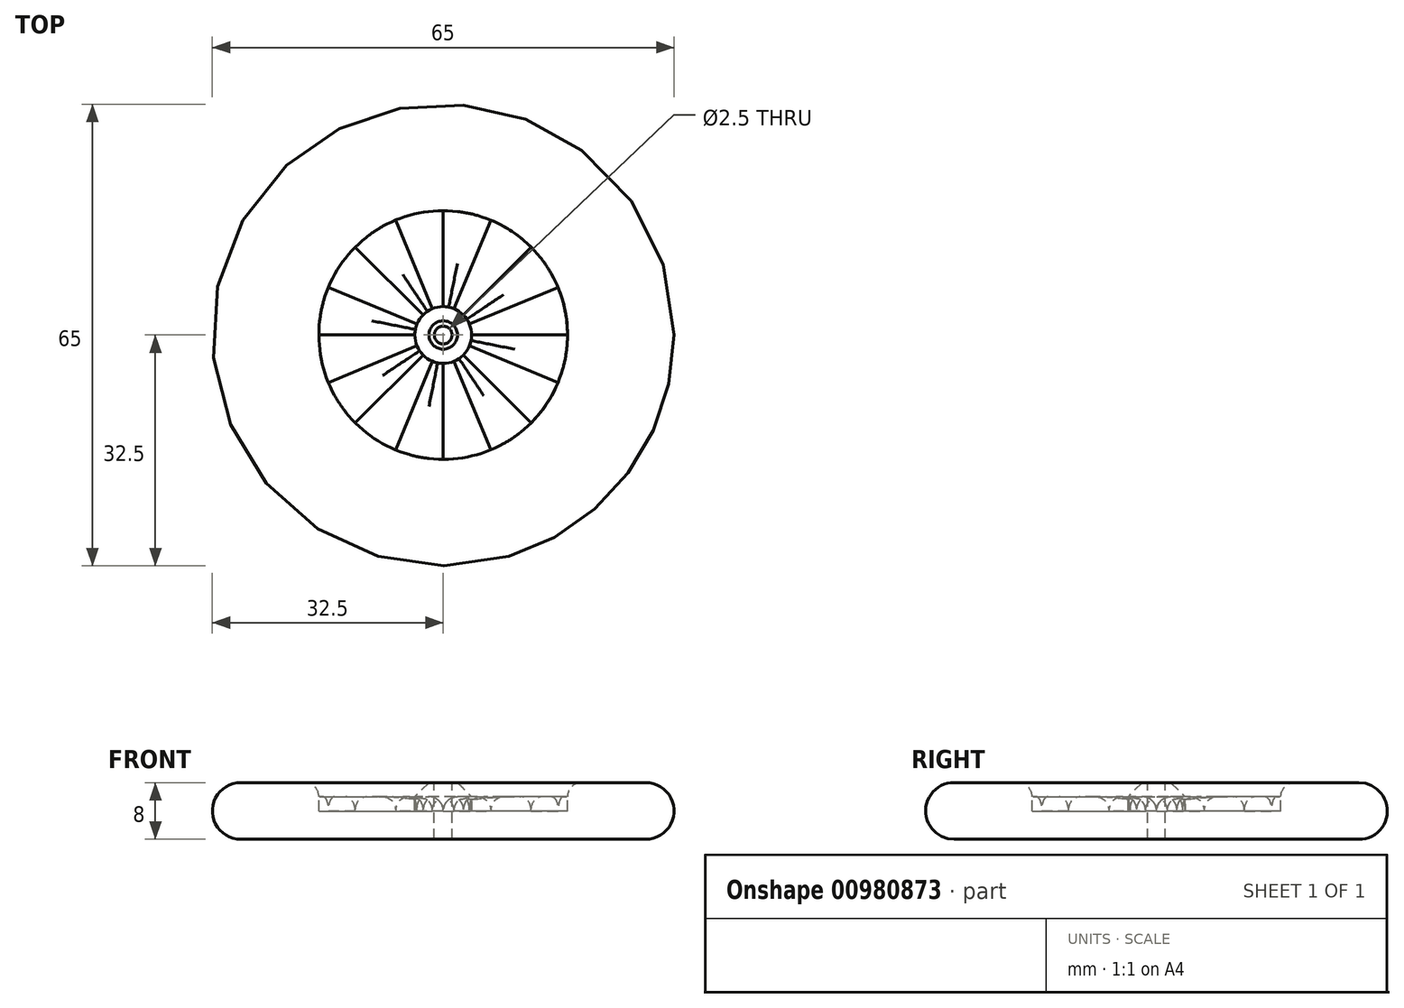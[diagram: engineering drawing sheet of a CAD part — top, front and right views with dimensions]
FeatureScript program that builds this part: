
annotation { "Feature Type Name" : "Feature", "Feature Type Description" : "" }
export const myFeature = defineFeature(function(context is Context, id is Id, definition is map)
    precondition{}
    {
        {
            var Q0;
            Q0=qCreatedBy(makeId("Top.planeOp"),FACE);
            var sketch = newSketch(context, id + "F0", { "sketchPlane" : qUnion([Q0])});
            skCircle(sketch, "E0", {"center": v(0, 0) * mm, "radius": 1.25 * mm});
            skCircle(sketch, "E1", {"center": v(0, 0) * mm, "radius": 4 * mm});
            skCircle(sketch, "E2", {"center": v(0, 0) * mm, "radius": 32.5 * mm});
            skCircle(sketch, "E3", {"center": v(0, 0) * mm, "radius": 17.5 * mm});
            skLineSegment(sketch, "E4", {"start": v(0, 17.5) * mm, "end": v(0, 4) * mm});
            skLineSegment(sketch, "E5.1.0", {"start": v(-6.7, 16.17) * mm, "end": v(-1.53, 3.7) * mm});
            skLineSegment(sketch, "E5.2.0", {"start": v(-12.37, 12.37) * mm, "end": v(-2.83, 2.83) * mm});
            skLineSegment(sketch, "E5.3.0", {"start": v(-16.17, 6.7) * mm, "end": v(-3.7, 1.53) * mm});
            skLineSegment(sketch, "E5.4.0", {"start": v(-17.5, 0) * mm, "end": v(-4, 0) * mm});
            skLineSegment(sketch, "E5.5.0", {"start": v(-16.17, -6.7) * mm, "end": v(-3.7, -1.53) * mm});
            skLineSegment(sketch, "E5.6.0", {"start": v(-12.37, -12.37) * mm, "end": v(-2.83, -2.83) * mm});
            skLineSegment(sketch, "E5.7.0", {"start": v(-6.7, -16.17) * mm, "end": v(-1.53, -3.7) * mm});
            skLineSegment(sketch, "E5.8.0", {"start": v(0, -17.5) * mm, "end": v(0, -4) * mm});
            skLineSegment(sketch, "E5.9.0", {"start": v(6.7, -16.17) * mm, "end": v(1.53, -3.7) * mm});
            skLineSegment(sketch, "E5.10.0", {"start": v(12.37, -12.37) * mm, "end": v(2.83, -2.83) * mm});
            skLineSegment(sketch, "E5.11.0", {"start": v(16.17, -6.7) * mm, "end": v(3.7, -1.53) * mm});
            skLineSegment(sketch, "E5.12.0", {"start": v(17.5, 0) * mm, "end": v(4, 0) * mm});
            skLineSegment(sketch, "E5.13.0", {"start": v(16.17, 6.7) * mm, "end": v(3.7, 1.53) * mm});
            skLineSegment(sketch, "E5.14.0", {"start": v(12.37, 12.37) * mm, "end": v(2.83, 2.83) * mm});
            skLineSegment(sketch, "E5.15.0", {"start": v(6.7, 16.17) * mm, "end": v(1.53, 3.7) * mm});
            skSolve(sketch);
        }
        {
            var Q0;
            Q0=makeQuery(id+"F0.imprint","IMPRINT",FACE,{"disambiguationData":[TD([[makeQuery(id+"F0.imprint","IMPRINT",EDGE,{"derivedFrom":sQuery(id+"F0.wireOp",EDGE,"E2")}),1.0]])]});
            var Q1;
            Q1=makeQuery(id+"F0.imprint","IMPRINT",FACE,{"disambiguationData":[TD([[makeQuery(id+"F0.imprint","IMPRINT",EDGE,{"derivedFrom":sQuery(id+"F0.wireOp",EDGE,"E0")}),-1.0]])]});
            extrude(context, id + "F1", {"entities" : qUnion([Q0, Q1]), "endBound" : BoundingType.SYMMETRIC, "oppositeDirection" : true, "depth" : 8 * mm, "offsetDistance" : 25 * mm});
        }
        {
            var Q0;
            Q0=makeQuery(id+"F0.imprint","IMPRINT",FACE,{"disambiguationData":[TD([[makeQuery(id+"F0.imprint","IMPRINT",EDGE,{"derivedFrom":sQuery(id+"F0.wireOp",EDGE,"E1")}),-1.0]])]});
            extrude(context, id + "F2", {"entities" : qUnion([Q0]), "operationType" : NewBodyOperationType.ADD, "oppositeDirection" : true, "depth" : 4 * mm, "offsetDistance" : 25 * mm});
        }
        {
            var Q0;
            {var subQ0=sQuery(id+"F0.wireOp",EDGE,"E5.3.0");Q0=makeQuery(id+"F0.imprint","IMPRINT",FACE,{"disambiguationData":[TD([[makeQuery(id+"F0.imprint","IMPRINT",EDGE,{"derivedFrom":subQ0}),-1.0]])]});}
            var Q1;
            {var subQ0=sQuery(id+"F0.wireOp",EDGE,"E5.1.0");Q1=makeQuery(id+"F0.imprint","IMPRINT",FACE,{"disambiguationData":[TD([[makeQuery(id+"F0.imprint","IMPRINT",EDGE,{"derivedFrom":subQ0}),-1.0]])]});}
            var Q2;
            {var subQ0=sQuery(id+"F0.wireOp",EDGE,"E4");Q2=makeQuery(id+"F0.imprint","IMPRINT",FACE,{"disambiguationData":[TD([[makeQuery(id+"F0.imprint","IMPRINT",EDGE,{"derivedFrom":subQ0}),1.0]])]});}
            var Q3;
            {var subQ0=sQuery(id+"F0.wireOp",EDGE,"E5.13.0");Q3=makeQuery(id+"F0.imprint","IMPRINT",FACE,{"disambiguationData":[TD([[makeQuery(id+"F0.imprint","IMPRINT",EDGE,{"derivedFrom":subQ0}),-1.0]])]});}
            var Q4;
            {var subQ0=sQuery(id+"F0.wireOp",EDGE,"E5.11.0");Q4=makeQuery(id+"F0.imprint","IMPRINT",FACE,{"disambiguationData":[TD([[makeQuery(id+"F0.imprint","IMPRINT",EDGE,{"derivedFrom":subQ0}),-1.0]])]});}
            var Q5;
            {var subQ0=sQuery(id+"F0.wireOp",EDGE,"E5.9.0");Q5=makeQuery(id+"F0.imprint","IMPRINT",FACE,{"disambiguationData":[TD([[makeQuery(id+"F0.imprint","IMPRINT",EDGE,{"derivedFrom":subQ0}),-1.0]])]});}
            var Q6;
            {var subQ0=sQuery(id+"F0.wireOp",EDGE,"E5.7.0");Q6=makeQuery(id+"F0.imprint","IMPRINT",FACE,{"disambiguationData":[TD([[makeQuery(id+"F0.imprint","IMPRINT",EDGE,{"derivedFrom":subQ0}),-1.0]])]});}
            var Q7;
            {var subQ0=sQuery(id+"F0.wireOp",EDGE,"E5.5.0");Q7=makeQuery(id+"F0.imprint","IMPRINT",FACE,{"disambiguationData":[TD([[makeQuery(id+"F0.imprint","IMPRINT",EDGE,{"derivedFrom":subQ0}),-1.0]])]});}
            extrude(context, id + "F3", {"entities" : qUnion([Q0, Q1, Q2, Q3, Q4, Q5, Q6, Q7]), "operationType" : NewBodyOperationType.ADD, "depth" : 2 * mm, "offsetDistance" : 25 * mm});
        }
        {
            var Q0;
            Q0=makeQuery(id+"F1.opExtrude","CAP_EDGE",EDGE,{"disambiguationData":[OSD([sQuery(id+"F0.wireOp",EDGE,"E2")])],"isStart":true});
            var Q1;
            Q1=makeQuery(id+"F1.opExtrude","CAP_EDGE",EDGE,{"disambiguationData":[OSD([sQuery(id+"F0.wireOp",EDGE,"E2")])],"isStart":false});
            fillet(context, id + "F4", {"entities" : qUnion([Q0, Q1]), "radius" : 4 * mm, "tangentPropagation" : true, "allowEdgeOverflow" : false});
        }
        {
            var Q0;
            Q0=makeQuery(id+"F1.opExtrude","CAP_EDGE",EDGE,{"disambiguationData":[OSD([sQuery(id+"F0.wireOp",EDGE,"E3")])],"isStart":true});
            var Q1;
            Q1=makeQuery(id+"F3.opExtrude","CAP_EDGE",EDGE,{"disambiguationData":[OSD([sQuery(id+"F0.wireOp",EDGE,"E5.5.0")])],"isStart":false});
            var Q2;
            Q2=makeQuery(id+"F3.opExtrude","CAP_EDGE",EDGE,{"disambiguationData":[OSD([sQuery(id+"F0.wireOp",EDGE,"E5.6.0")])],"isStart":false});
            var Q3;
            Q3=makeQuery(id+"F3.opExtrude","CAP_EDGE",EDGE,{"disambiguationData":[OSD([sQuery(id+"F0.wireOp",EDGE,"E5.4.0")])],"isStart":false});
            var Q4;
            Q4=makeQuery(id+"F3.opExtrude","CAP_EDGE",EDGE,{"disambiguationData":[OSD([sQuery(id+"F0.wireOp",EDGE,"E5.3.0")])],"isStart":false});
            var Q5;
            Q5=makeQuery(id+"F3.opExtrude","CAP_EDGE",EDGE,{"disambiguationData":[OSD([sQuery(id+"F0.wireOp",EDGE,"E5.2.0")])],"isStart":false});
            var Q6;
            Q6=makeQuery(id+"F3.opExtrude","CAP_EDGE",EDGE,{"disambiguationData":[OSD([sQuery(id+"F0.wireOp",EDGE,"E5.1.0")])],"isStart":false});
            var Q7;
            Q7=makeQuery(id+"F3.opExtrude","CAP_EDGE",EDGE,{"disambiguationData":[OSD([sQuery(id+"F0.wireOp",EDGE,"E4")])],"isStart":false});
            var Q8;
            Q8=makeQuery(id+"F3.opExtrude","CAP_EDGE",EDGE,{"disambiguationData":[OSD([sQuery(id+"F0.wireOp",EDGE,"E5.15.0")])],"isStart":false});
            var Q9;
            Q9=makeQuery(id+"F3.opExtrude","CAP_EDGE",EDGE,{"disambiguationData":[OSD([sQuery(id+"F0.wireOp",EDGE,"E5.14.0")])],"isStart":false});
            var Q10;
            Q10=makeQuery(id+"F3.opExtrude","CAP_EDGE",EDGE,{"disambiguationData":[OSD([sQuery(id+"F0.wireOp",EDGE,"E5.13.0")])],"isStart":false});
            var Q11;
            Q11=makeQuery(id+"F3.opExtrude","CAP_EDGE",EDGE,{"disambiguationData":[OSD([sQuery(id+"F0.wireOp",EDGE,"E5.12.0")])],"isStart":false});
            var Q12;
            Q12=makeQuery(id+"F3.opExtrude","CAP_EDGE",EDGE,{"disambiguationData":[OSD([sQuery(id+"F0.wireOp",EDGE,"E5.11.0")])],"isStart":false});
            var Q13;
            Q13=makeQuery(id+"F3.opExtrude","CAP_EDGE",EDGE,{"disambiguationData":[OSD([sQuery(id+"F0.wireOp",EDGE,"E5.10.0")])],"isStart":false});
            var Q14;
            Q14=makeQuery(id+"F3.opExtrude","CAP_EDGE",EDGE,{"disambiguationData":[OSD([sQuery(id+"F0.wireOp",EDGE,"E5.9.0")])],"isStart":false});
            var Q15;
            Q15=makeQuery(id+"F3.opExtrude","CAP_EDGE",EDGE,{"disambiguationData":[OSD([sQuery(id+"F0.wireOp",EDGE,"E5.8.0")])],"isStart":false});
            var Q16;
            Q16=makeQuery(id+"F3.opExtrude","CAP_EDGE",EDGE,{"disambiguationData":[OSD([sQuery(id+"F0.wireOp",EDGE,"E5.7.0")])],"isStart":false});
            fillet(context, id + "F5", {"entities" : qUnion([Q0, Q1, Q2, Q3, Q4, Q5, Q6, Q7, Q8, Q9, Q10, Q11, Q12, Q13, Q14, Q15, Q16]), "radius" : 2 * mm, "tangentPropagation" : true, "allowEdgeOverflow" : false});
        }
        {
            var Q0;
            Q0=makeQuery(id+"F1.opExtrude","CAP_EDGE",EDGE,{"disambiguationData":[OSD([sQuery(id+"F0.wireOp",EDGE,"E1")])],"isStart":true});
            chamfer(context, id + "F6", {"entities" : qUnion([Q0]), "width" : 2 * mm, "tangentPropagation" : true});
        }
    });
